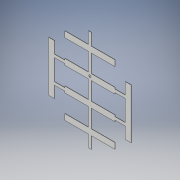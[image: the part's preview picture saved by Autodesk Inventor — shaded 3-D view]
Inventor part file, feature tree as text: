
AUTODESK INVENTOR PART (.ipt)
format: ipt  version: 2019 (Build 230136000, 136)  size: 367,616 bytes
history: native  units: mm
features: extrude x2, sketch x2
ambient origin geometry x8: Origin, YZ Plane, XZ Plane, XY Plane, X Axis, Y Axis, Z Axis, Center Point
bodies: Solid1 (feature_tree)
feature tree (4):
  extrude  "Extrusion1"  Depth=85.0mm
  extrude  "Extrusion2"  Depth=40.0mm
  sketch  "Sketch1"  dims[d0=172.0mm d12=85.0mm]
  sketch  "Sketch2"  dims[d13=10.0mm d14=40.0mm d16=40.5mm d17=10.0mm d19=10.0mm d21=20.25mm d22=20.25mm d23=30.5mm d24=10.0mm d25=85.0mm d26=20.961916mm d27=65.0mm d28=5.0mm d29=5.0mm d30=5.0mm d31=0.5mm d32=0.0mm d33=4.0mm d34=10.0mm d35=0.0mm]
